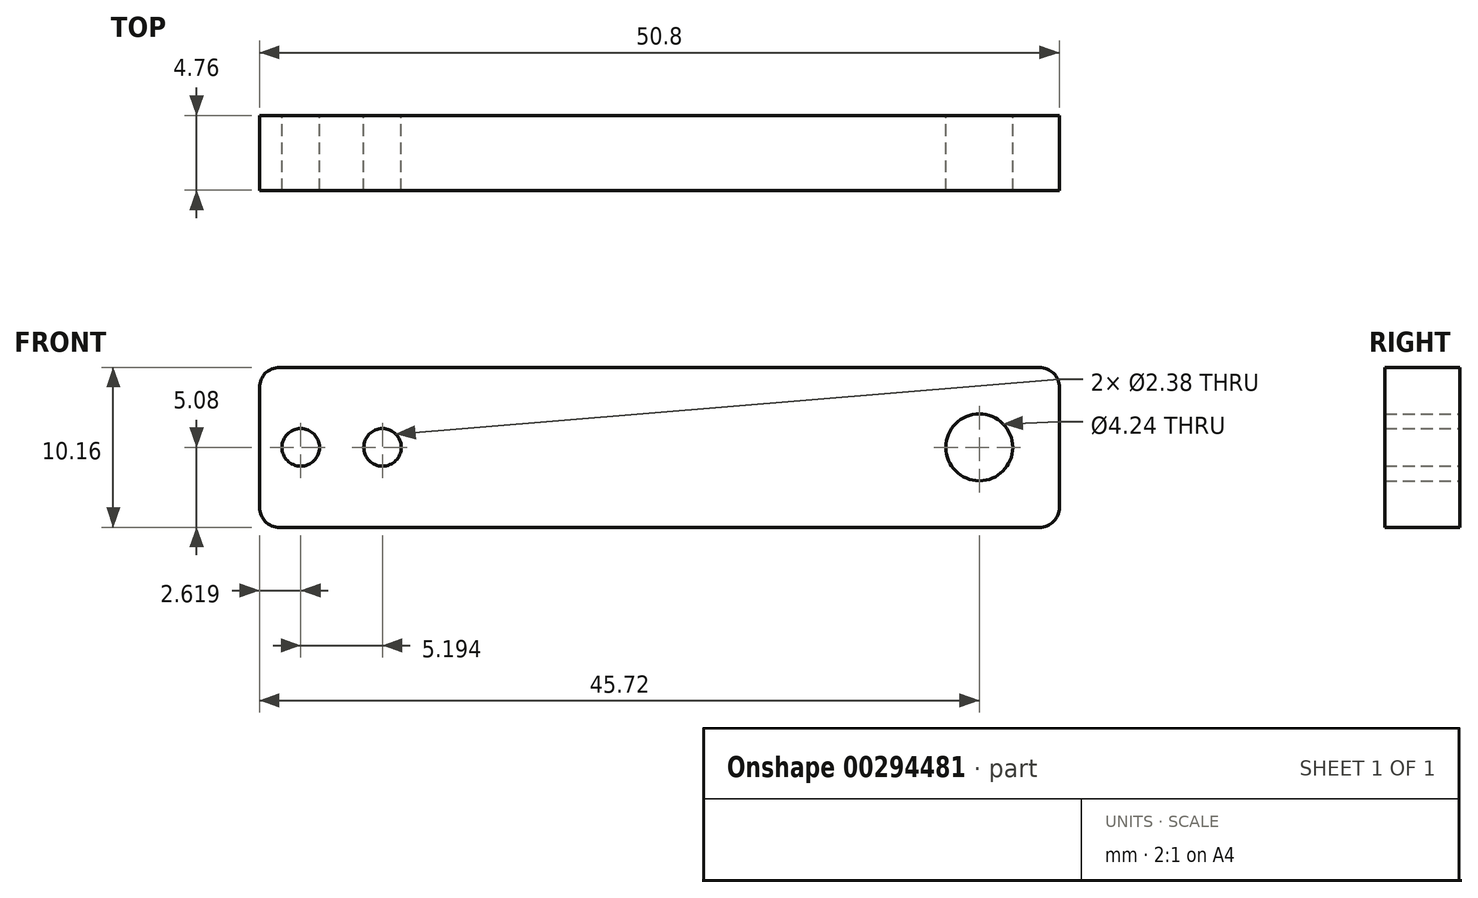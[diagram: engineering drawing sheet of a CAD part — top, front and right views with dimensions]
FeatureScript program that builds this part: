
annotation { "Feature Type Name" : "Feature", "Feature Type Description" : "" }
export const myFeature = defineFeature(function(context is Context, id is Id, definition is map)
    precondition{}
    {
        {
            var Q0;
            Q0=qCreatedBy(makeId("Front.planeOp"),FACE);
            var sketch = newSketch(context, id + "F0", { "sketchPlane" : qUnion([Q0])});
            skLineSegment(sketch, "E0.bottom", {"start": v(25.4, 5.08) * mm, "end": v(-25.4, 5.08) * mm});
            skLineSegment(sketch, "E0.top", {"start": v(25.4, -5.08) * mm, "end": v(-25.4, -5.08) * mm});
            skLineSegment(sketch, "E0.left", {"start": v(25.4, 5.08) * mm, "end": v(25.4, -5.08) * mm});
            skLineSegment(sketch, "E0.right", {"start": v(-25.4, 5.08) * mm, "end": v(-25.4, -5.08) * mm});
            skPoint(sketch, "E0.middle", {"position": v(0, 0) * mm});
            skCircle(sketch, "E1", {"center": v(20.32, 0) * mm, "radius": 2.12 * mm});
            skCircle(sketch, "E2", {"center": v(-17.59, 0) * mm, "radius": 1.2 * mm});
            skCircle(sketch, "E3", {"center": v(-22.78, 0) * mm, "radius": 1.2 * mm});
            skSolve(sketch);
        }
        {
            var Q0;
            Q0=makeQuery(id+"F0.imprint","IMPRINT",FACE,{"disambiguationData":[TD([[makeQuery(id+"F0.imprint","IMPRINT",EDGE,{"derivedFrom":sQuery(id+"F0.wireOp",EDGE,"E0.bottom")}),1.0]])]});
            extrude(context, id + "F1", {"entities" : qUnion([Q0]), "depth" : 4.76 * mm});
        }
        {
            var Q0;
            Q0=makeQuery(id+"F1.opExtrude","SWEPT_EDGE",EDGE,{"disambiguationData":[OSD([sQuery(id+"F0.wireOp",EDGE,"E0.bottom"),sQuery(id+"F0.wireOp",EDGE,"E0.right")])]});
            var Q1;
            Q1=makeQuery(id+"F1.opExtrude","SWEPT_EDGE",EDGE,{"disambiguationData":[OSD([sQuery(id+"F0.wireOp",EDGE,"E0.bottom"),sQuery(id+"F0.wireOp",EDGE,"E0.left")])]});
            var Q2;
            Q2=makeQuery(id+"F1.opExtrude","SWEPT_EDGE",EDGE,{"disambiguationData":[OSD([sQuery(id+"F0.wireOp",EDGE,"E0.top"),sQuery(id+"F0.wireOp",EDGE,"E0.left")])]});
            var Q3;
            Q3=makeQuery(id+"F1.opExtrude","SWEPT_EDGE",EDGE,{"disambiguationData":[OSD([sQuery(id+"F0.wireOp",EDGE,"E0.top"),sQuery(id+"F0.wireOp",EDGE,"E0.right")])]});
            fillet(context, id + "F2", {"entities" : qUnion([Q0, Q1, Q2, Q3]), "radius" : 1.27 * mm, "tangentPropagation" : true, "allowEdgeOverflow" : false});
        }
    });
